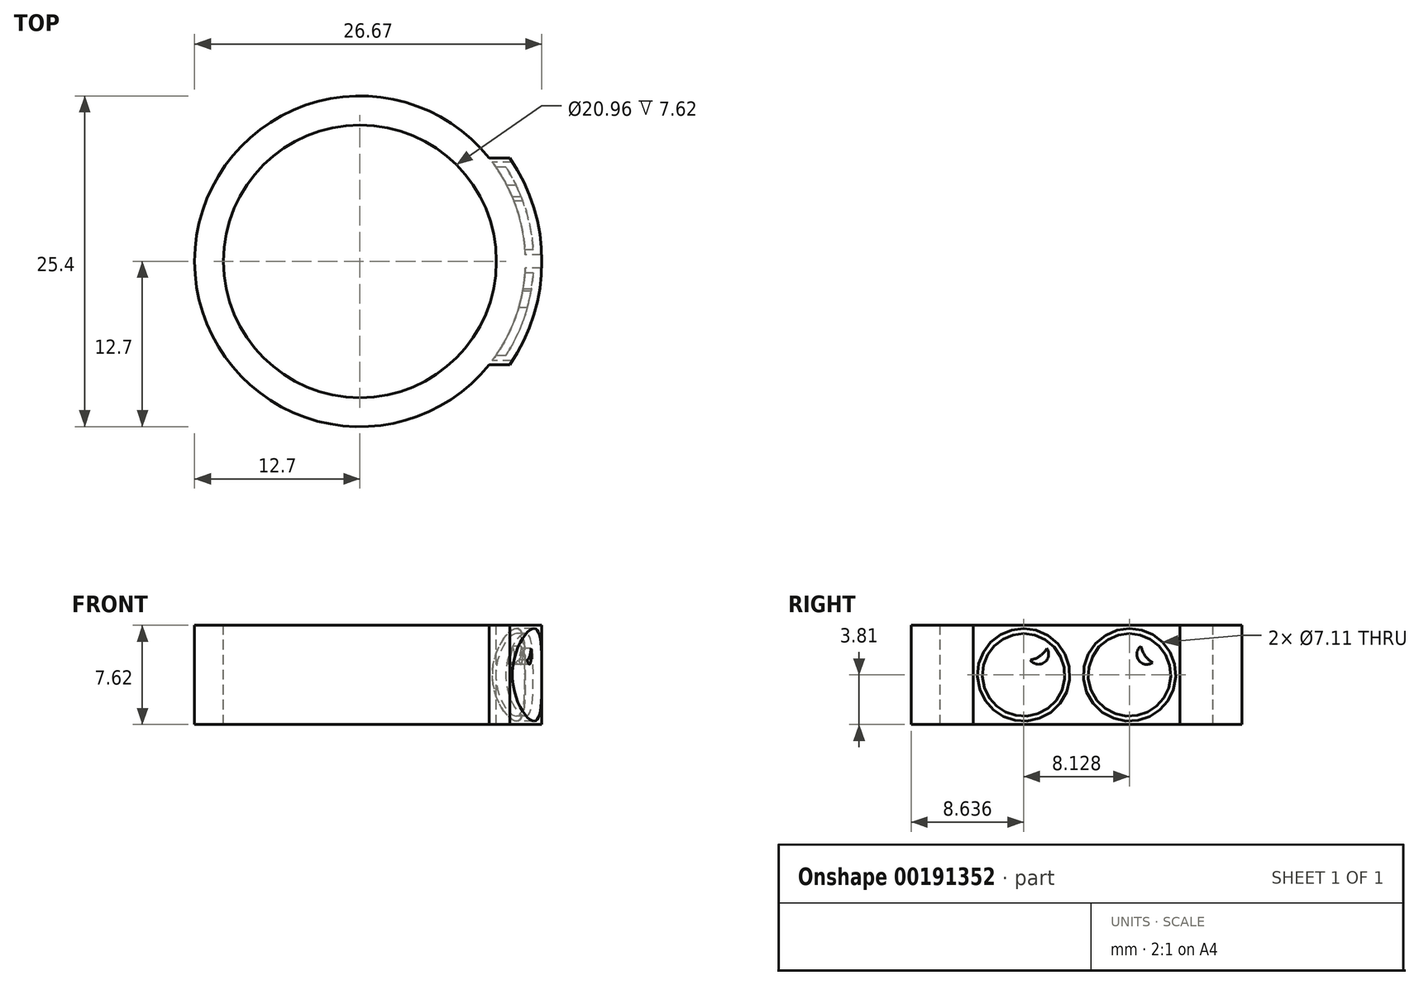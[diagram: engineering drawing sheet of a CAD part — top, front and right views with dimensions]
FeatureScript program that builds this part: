
annotation { "Feature Type Name" : "Feature", "Feature Type Description" : "" }
export const myFeature = defineFeature(function(context is Context, id is Id, definition is map)
    precondition{}
    {
        {
            var Q0;
            Q0=qCreatedBy(makeId("Top.planeOp"),FACE);
            var sketch = newSketch(context, id + "F0", { "sketchPlane" : qUnion([Q0])});
            skCircle(sketch, "E0", {"center": v(0, 0) * mm, "radius": 12.7 * mm});
            skCircle(sketch, "E1.0", {"center": v(0, 0) * mm, "radius": 10.16 * mm});
            skSolve(sketch);
        }
        {
            var Q0;
            Q0=makeQuery(id+"F0.imprint","IMPRINT",FACE,{"disambiguationData":[TD([[makeQuery(id+"F0.imprint","IMPRINT",EDGE,{"derivedFrom":sQuery(id+"F0.wireOp",EDGE,"E0")}),1.0]])]});
            extrude(context, id + "F1", {"entities" : qUnion([Q0]), "depth" : 7.62 * mm});
        }
        {
            var Q0;
            Q0=qCreatedBy(makeId("Right.planeOp"),FACE);
            var sketch = newSketch(context, id + "F2", { "sketchPlane" : qUnion([Q0])});
            skCircle(sketch, "E2", {"center": v(-4.06, 3.81) * mm, "radius": 3.17 * mm});
            skLineSegment(sketch, "E3", {"start": v(-4.06, 3.81) * mm, "end": v(-4.06, 16.46) * mm, "construction": true});
            skPoint(sketch, "E4", {"position": v(-5.84, 5.84) * mm});
            skPoint(sketch, "E5", {"position": v(-4.57, 4.95) * mm});
            skArc(sketch, "E6", {"start": v(-5.84, 5.84) * mm, "mid": v(-5.3, 5.25) * mm, "end": v(-4.57, 4.95) * mm});
            skArc(sketch, "E7", {"start": v(-5.84, 5.84) * mm, "mid": v(-5.65, 4.76) * mm, "end": v(-4.57, 4.95) * mm});
            skArc(sketch, "E8.MirrorCS", {"start": v(-2.29, 5.84) * mm, "mid": v(-2.82, 5.25) * mm, "end": v(-3.56, 4.95) * mm});
            skArc(sketch, "E9.MirrorCS", {"start": v(-2.29, 5.84) * mm, "mid": v(-2.48, 4.76) * mm, "end": v(-3.56, 4.95) * mm});
            skCircle(sketch, "E10.0", {"center": v(-4.06, 3.81) * mm, "radius": 3.56 * mm});
            skPoint(sketch, "E11.start.orphan", {"position": v(0, 8.18) * mm});
            skLineSegment(sketch, "E12", {"start": v(-4.06, 3.81) * mm, "end": v(-7.24, 3.81) * mm, "construction": true});
            skLineSegment(sketch, "E13", {"start": v(-4.06, 3.81) * mm, "end": v(-0.89, 3.81) * mm, "construction": true});
            skArc(sketch, "E14", {"start": v(-7.24, 3.81) * mm, "mid": v(-6.7, 3.42) * mm, "end": v(-6.1, 3.1) * mm});
            skLineSegment(sketch, "E15", {"start": v(-6.1, 3.1) * mm, "end": v(-6.1, 1.37) * mm});
            skLineSegment(sketch, "E16", {"start": v(-5.84, 3) * mm, "end": v(-5.84, 1.18) * mm});
            skArc(sketch, "E17.trimOffspring", {"start": v(-5.84, 3) * mm, "mid": v(-5.4, 2.86) * mm, "end": v(-4.95, 2.76) * mm});
            skLineSegment(sketch, "E18", {"start": v(-4.95, 2.76) * mm, "end": v(-4.95, 0.76) * mm});
            skLineSegment(sketch, "E19", {"start": v(-4.7, 2.72) * mm, "end": v(-4.7, 0.7) * mm});
            skArc(sketch, "E20.trimOffspring", {"start": v(-4.7, 2.72) * mm, "mid": v(-4.06, 2.68) * mm, "end": v(-3.43, 2.72) * mm});
            skLineSegment(sketch, "E21.MirrorCS", {"start": v(-3.43, 2.72) * mm, "end": v(-3.43, 0.7) * mm});
            skLineSegment(sketch, "E22.MirrorCS", {"start": v(-3.18, 2.76) * mm, "end": v(-3.18, 0.76) * mm});
            skLineSegment(sketch, "E23.MirrorCS", {"start": v(-2.29, 3) * mm, "end": v(-2.29, 1.18) * mm});
            skLineSegment(sketch, "E24.MirrorCS", {"start": v(-2.03, 3.1) * mm, "end": v(-2.03, 1.37) * mm});
            skArc(sketch, "E25.trimOffspring", {"start": v(-3.18, 2.76) * mm, "mid": v(-2.72, 2.86) * mm, "end": v(-2.29, 3) * mm});
            skArc(sketch, "E26.trimOffspring", {"start": v(-2.03, 3.1) * mm, "mid": v(-1.44, 3.42) * mm, "end": v(-0.89, 3.81) * mm});
            skLineSegment(sketch, "E27", {"start": v(0, 8.18) * mm, "end": v(0, 0) * mm, "construction": true});
            skCircle(sketch, "E28.MirrorC", {"center": v(4.06, 3.81) * mm, "radius": 3.56 * mm});
            skCircle(sketch, "E29.MirrorC", {"center": v(4.06, 3.81) * mm, "radius": 3.17 * mm});
            skArc(sketch, "E30.MirrorCS", {"start": v(2.29, 4.75) * mm, "mid": v(2.88, 5.28) * mm, "end": v(3.18, 6.02) * mm});
            skArc(sketch, "E31.MirrorCS", {"start": v(2.29, 4.75) * mm, "mid": v(3.37, 4.94) * mm, "end": v(3.17, 6.02) * mm});
            skArc(sketch, "E32.MirrorCS", {"start": v(5.84, 4.75) * mm, "mid": v(5.25, 5.28) * mm, "end": v(4.95, 6.02) * mm});
            skArc(sketch, "E33.MirrorCS", {"start": v(5.84, 4.75) * mm, "mid": v(4.76, 4.94) * mm, "end": v(4.95, 6.02) * mm});
            skLineSegment(sketch, "E34", {"start": v(4.06, 3.81) * mm, "end": v(0.89, 3.81) * mm, "construction": true});
            skArc(sketch, "E35", {"start": v(6.97, 2.54) * mm, "mid": v(6.45, 3.02) * mm, "end": v(5.84, 3.39) * mm});
            skArc(sketch, "E36", {"start": v(6.5, 1.78) * mm, "mid": v(6.18, 1.95) * mm, "end": v(5.84, 2.1) * mm});
            skLineSegment(sketch, "E37", {"start": v(4.06, 3.81) * mm, "end": v(4.06, -0.16) * mm, "construction": true});
            skLineSegment(sketch, "E38", {"start": v(3.57, 3.78) * mm, "end": v(3.57, 2.4) * mm});
            skLineSegment(sketch, "E39", {"start": v(3.31, 3.74) * mm, "end": v(3.31, 2.37) * mm});
            skLineSegment(sketch, "E40", {"start": v(2.54, 3.5) * mm, "end": v(2.54, 2.19) * mm});
            skLineSegment(sketch, "E41", {"start": v(2.28, 3.39) * mm, "end": v(2.28, 2.1) * mm});
            skLineSegment(sketch, "E42.MirrorCS", {"start": v(4.56, 3.78) * mm, "end": v(4.56, 2.4) * mm});
            skLineSegment(sketch, "E43.MirrorCS", {"start": v(4.81, 3.74) * mm, "end": v(4.81, 2.37) * mm});
            skLineSegment(sketch, "E44.MirrorCS", {"start": v(5.59, 3.5) * mm, "end": v(5.59, 2.19) * mm});
            skLineSegment(sketch, "E45.MirrorCS", {"start": v(5.84, 3.39) * mm, "end": v(5.84, 2.1) * mm});
            skArc(sketch, "E46.trimOffspring", {"start": v(3.31, 3.74) * mm, "mid": v(2.92, 3.64) * mm, "end": v(2.54, 3.5) * mm});
            skArc(sketch, "E47.trimOffspring", {"start": v(2.28, 3.39) * mm, "mid": v(1.68, 3.02) * mm, "end": v(1.15, 2.54) * mm});
            skArc(sketch, "E48.trimOffspring", {"start": v(2.28, 2.1) * mm, "mid": v(1.95, 1.95) * mm, "end": v(1.62, 1.78) * mm});
            skArc(sketch, "E49.trimOffspring", {"start": v(3.31, 2.37) * mm, "mid": v(2.92, 2.3) * mm, "end": v(2.54, 2.19) * mm});
            skArc(sketch, "E50.trimOffspring", {"start": v(4.56, 2.4) * mm, "mid": v(4.06, 2.43) * mm, "end": v(3.57, 2.4) * mm});
            skArc(sketch, "E51.trimOffspring", {"start": v(4.56, 3.78) * mm, "mid": v(4.06, 3.81) * mm, "end": v(3.57, 3.78) * mm});
            skArc(sketch, "E52.trimOffspring", {"start": v(5.59, 3.5) * mm, "mid": v(5.2, 3.64) * mm, "end": v(4.81, 3.74) * mm});
            skArc(sketch, "E53.trimOffspring", {"start": v(5.59, 2.19) * mm, "mid": v(5.2, 2.3) * mm, "end": v(4.81, 2.37) * mm});
            skLineSegment(sketch, "E54.bottom", {"start": v(-7.94, 7.62) * mm, "end": v(7.94, 7.62) * mm});
            skLineSegment(sketch, "E54.top", {"start": v(-7.94, 0) * mm, "end": v(7.94, 0) * mm});
            skLineSegment(sketch, "E54.left", {"start": v(-7.94, 7.62) * mm, "end": v(-7.94, 0) * mm});
            skLineSegment(sketch, "E54.right", {"start": v(7.94, 7.62) * mm, "end": v(7.94, 0) * mm});
            skSolve(sketch);
        }
        {
            var Q0;
            Q0=makeQuery(id+"F2.imprint","IMPRINT",FACE,{"disambiguationData":[TD([[makeQuery(id+"F2.imprint","IMPRINT",EDGE,{"derivedFrom":sQuery(id+"F2.wireOp",EDGE,"E8.MirrorCS")}),1.0]])]});
            var Q1;
            Q1=makeQuery(id+"F2.imprint","IMPRINT",FACE,{"disambiguationData":[TD([[makeQuery(id+"F2.imprint","IMPRINT",EDGE,{"derivedFrom":sQuery(id+"F2.wireOp",EDGE,"E6")}),-1.0]])]});
            var Q2;
            {var subQ0=sQuery(id+"F2.wireOp",EDGE,"E14");Q2=makeQuery(id+"F2.imprint","IMPRINT",FACE,{"disambiguationData":[TD([[makeQuery(id+"F2.imprint","IMPRINT",EDGE,{"derivedFrom":subQ0}),-1.0]])]});}
            var Q3;
            {var subQ0=sQuery(id+"F2.wireOp",EDGE,"E16");Q3=makeQuery(id+"F2.imprint","IMPRINT",FACE,{"disambiguationData":[TD([[makeQuery(id+"F2.imprint","IMPRINT",EDGE,{"derivedFrom":subQ0}),1.0]])]});}
            var Q4;
            {var subQ0=sQuery(id+"F2.wireOp",EDGE,"E19");Q4=makeQuery(id+"F2.imprint","IMPRINT",FACE,{"disambiguationData":[TD([[makeQuery(id+"F2.imprint","IMPRINT",EDGE,{"derivedFrom":subQ0}),1.0]])]});}
            var Q5;
            {var subQ0=sQuery(id+"F2.wireOp",EDGE,"E22.MirrorCS");Q5=makeQuery(id+"F2.imprint","IMPRINT",FACE,{"disambiguationData":[TD([[makeQuery(id+"F2.imprint","IMPRINT",EDGE,{"derivedFrom":subQ0}),1.0]])]});}
            var Q6;
            {var subQ0=sQuery(id+"F2.wireOp",EDGE,"E24.MirrorCS");Q6=makeQuery(id+"F2.imprint","IMPRINT",FACE,{"disambiguationData":[TD([[makeQuery(id+"F2.imprint","IMPRINT",EDGE,{"derivedFrom":subQ0}),1.0]])]});}
            var Q7;
            Q7=makeQuery(id+"F2.imprint","IMPRINT",FACE,{"disambiguationData":[TD([[makeQuery(id+"F2.imprint","IMPRINT",EDGE,{"derivedFrom":sQuery(id+"F2.wireOp",EDGE,"E30.MirrorCS")}),-1.0]])]});
            var Q8;
            Q8=makeQuery(id+"F2.imprint","IMPRINT",FACE,{"disambiguationData":[TD([[makeQuery(id+"F2.imprint","IMPRINT",EDGE,{"derivedFrom":sQuery(id+"F2.wireOp",EDGE,"E32.MirrorCS")}),1.0]])]});
            var Q9;
            Q9=makeQuery(id+"F2.imprint","IMPRINT",FACE,{"disambiguationData":[TD([[makeQuery(id+"F2.imprint","IMPRINT",EDGE,{"derivedFrom":sQuery(id+"F2.wireOp",EDGE,"E41")}),-1.0]])]});
            var Q10;
            Q10=makeQuery(id+"F2.imprint","IMPRINT",FACE,{"disambiguationData":[TD([[makeQuery(id+"F2.imprint","IMPRINT",EDGE,{"derivedFrom":sQuery(id+"F2.wireOp",EDGE,"E39")}),-1.0]])]});
            var Q11;
            Q11=makeQuery(id+"F2.imprint","IMPRINT",FACE,{"disambiguationData":[TD([[makeQuery(id+"F2.imprint","IMPRINT",EDGE,{"derivedFrom":sQuery(id+"F2.wireOp",EDGE,"E38")}),1.0]])]});
            var Q12;
            Q12=makeQuery(id+"F2.imprint","IMPRINT",FACE,{"disambiguationData":[TD([[makeQuery(id+"F2.imprint","IMPRINT",EDGE,{"derivedFrom":sQuery(id+"F2.wireOp",EDGE,"E43.MirrorCS")}),1.0]])]});
            var Q13;
            {var subQ0=sQuery(id+"F2.wireOp",EDGE,"E35");Q13=makeQuery(id+"F2.imprint","IMPRINT",FACE,{"disambiguationData":[TD([[makeQuery(id+"F2.imprint","IMPRINT",EDGE,{"derivedFrom":subQ0}),1.0]])]});}
            extrude(context, id + "F3", {"entities" : qUnion([Q0, Q1, Q2, Q3, Q4, Q5, Q6, Q7, Q8, Q9, Q10, Q11, Q12, Q13]), "operationType" : NewBodyOperationType.ADD, "depth" : 25.4 * mm});
        }
        {
            var Q0;
            Q0=makeQuery(id+"F1.opExtrude","CAP_FACE",FACE,{"disambiguationData":[OSD([sQuery(id+"F0.wireOp",EDGE,"E0"),sQuery(id+"F0.wireOp",EDGE,"E1.0")])],"isStart":false});
            var sketch = newSketch(context, id + "F4", { "sketchPlane" : qUnion([Q0])});
            skCircle(sketch, "E55", {"center": v(0, 0) * mm, "radius": 10.16 * mm});
            skCircle(sketch, "E56", {"center": v(0, 0) * mm, "radius": 13.34 * mm});
            skCircle(sketch, "E57", {"center": v(0, 0) * mm, "radius": 38.74 * mm});
            skSolve(sketch);
        }
        {
            var Q0;
            Q0=makeQuery(id+"F4.imprint","IMPRINT",FACE,{"disambiguationData":[TD([[makeQuery(id+"F4.imprint","IMPRINT",EDGE,{"derivedFrom":sQuery(id+"F4.wireOp",EDGE,"E56")}),-1.0]])]});
            var Q1;
            Q1=makeQuery(id+"F4.imprint","IMPRINT",FACE,{"disambiguationData":[TD([[makeQuery(id+"F4.imprint","IMPRINT",EDGE,{"derivedFrom":sQuery(id+"F4.wireOp",EDGE,"E55")}),1.0]])]});
            extrude(context, id + "F5", {"entities" : qUnion([Q0, Q1]), "operationType" : NewBodyOperationType.REMOVE, "endBound" : BoundingType.THROUGH_ALL, "oppositeDirection" : true, "depth" : 25.4 * mm});
        }
        {
            var Q0;
            Q0 = qSketchRegion(id + "F2", true);
            extrude(context, id + "F6", {"entities" : qUnion([Q0]), "operationType" : NewBodyOperationType.ADD, "depth" : 25.4 * mm});
        }
        {
            var Q0;
            Q0=makeQuery(id+"F1.opExtrude","CAP_FACE",FACE,{"disambiguationData":[OSD([sQuery(id+"F0.wireOp",EDGE,"E0"),sQuery(id+"F0.wireOp",EDGE,"E1.0")])],"isStart":false});
            var sketch = newSketch(context, id + "F7", { "sketchPlane" : qUnion([Q0])});
            skCircle(sketch, "E58", {"center": v(0, 0) * mm, "radius": 10.16 * mm});
            skCircle(sketch, "E59", {"center": v(0, 0) * mm, "radius": 13.97 * mm});
            skCircle(sketch, "E60", {"center": v(0, 0) * mm, "radius": 31.75 * mm});
            skSolve(sketch);
        }
        {
            var Q0;
            Q0=makeQuery(id+"F7.imprint","IMPRINT",FACE,{"disambiguationData":[TD([[makeQuery(id+"F7.imprint","IMPRINT",EDGE,{"derivedFrom":sQuery(id+"F7.wireOp",EDGE,"E58")}),1.0]])]});
            var Q1;
            Q1=makeQuery(id+"F7.imprint","IMPRINT",FACE,{"disambiguationData":[TD([[makeQuery(id+"F7.imprint","IMPRINT",EDGE,{"derivedFrom":sQuery(id+"F7.wireOp",EDGE,"E59")}),-1.0]])]});
            extrude(context, id + "F8", {"entities" : qUnion([Q0, Q1]), "operationType" : NewBodyOperationType.REMOVE, "endBound" : BoundingType.THROUGH_ALL, "oppositeDirection" : true, "depth" : 25.4 * mm});
        }
        {
            var Q0;
            Q0=makeQuery(id+"F1.opExtrude","CAP_FACE",FACE,{"disambiguationData":[OSD([sQuery(id+"F0.wireOp",EDGE,"E0"),sQuery(id+"F0.wireOp",EDGE,"E1.0")])],"isStart":false});
            var sketch = newSketch(context, id + "F9", { "sketchPlane" : qUnion([Q0])});
            skCircle(sketch, "E61", {"center": v(0, 0) * mm, "radius": 10.48 * mm});
            skSolve(sketch);
        }
        {
            var Q0;
            Q0 = qSketchRegion(id + "F9", true);
            extrude(context, id + "F10", {"entities" : qUnion([Q0]), "operationType" : NewBodyOperationType.REMOVE, "endBound" : BoundingType.THROUGH_ALL, "oppositeDirection" : true, "depth" : 25.4 * mm});
        }
    });
